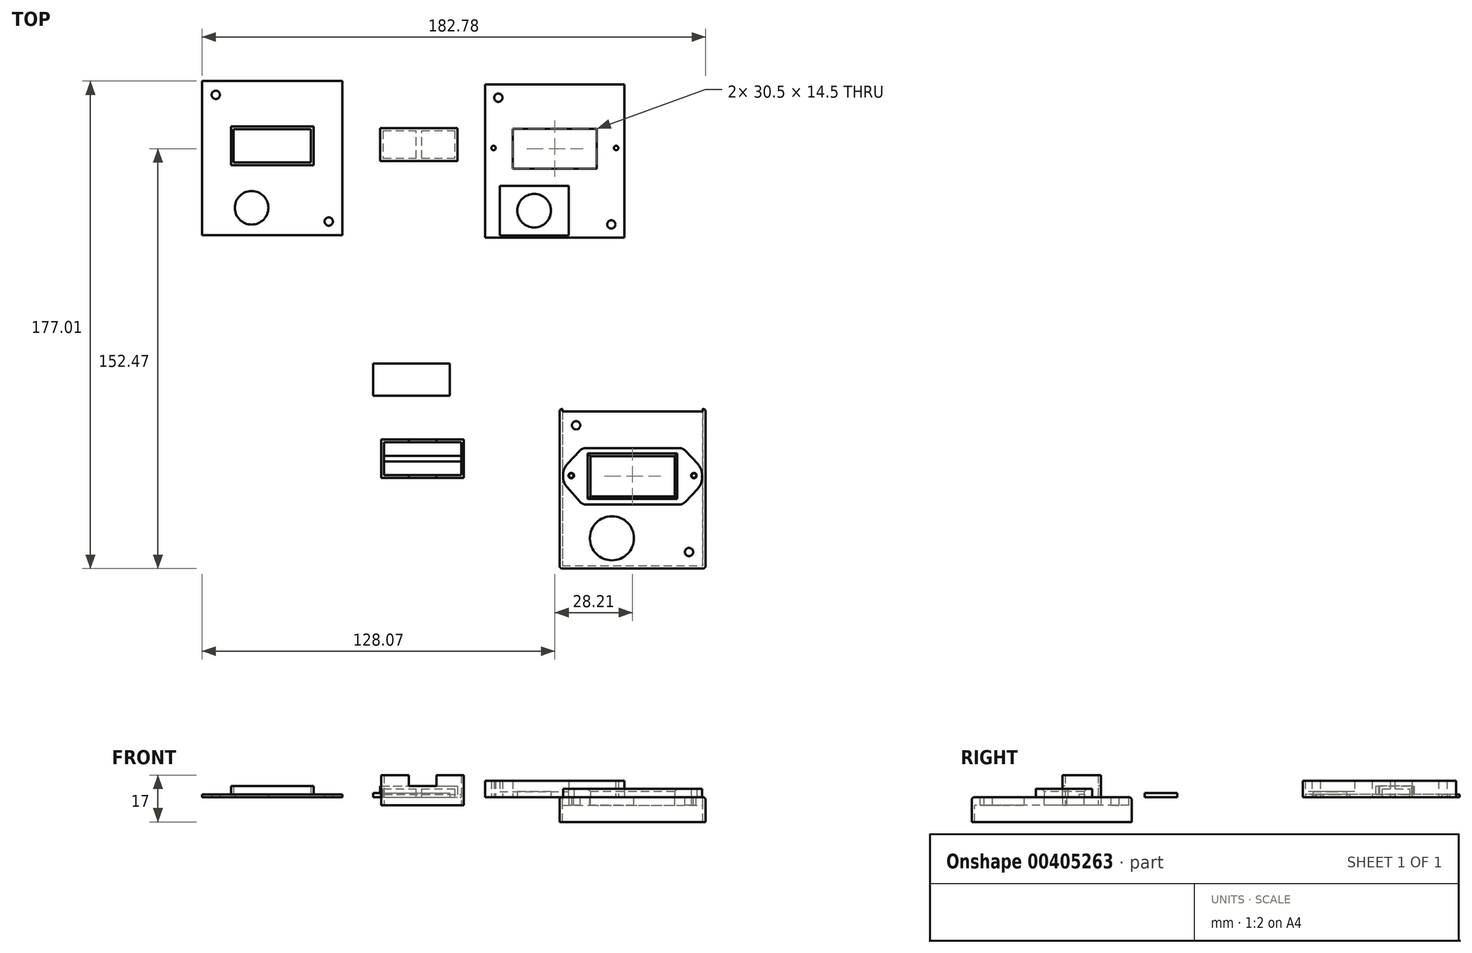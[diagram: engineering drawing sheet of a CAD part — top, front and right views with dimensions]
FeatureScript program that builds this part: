
annotation { "Feature Type Name" : "Feature", "Feature Type Description" : "" }
export const myFeature = defineFeature(function(context is Context, id is Id, definition is map)
    precondition{}
    {
        {
            var Q0;
            Q0=qCreatedBy(makeId("Top.planeOp"),FACE);
            var sketch = newSketch(context, id + "F0", { "sketchPlane" : qUnion([Q0])});
            skLineSegment(sketch, "E0.bottom", {"start": v(25.5, 28) * mm, "end": v(-25.5, 28) * mm});
            skLineSegment(sketch, "E0.top", {"start": v(25.5, -28) * mm, "end": v(-25.5, -28) * mm});
            skLineSegment(sketch, "E0.left", {"start": v(25.5, 28) * mm, "end": v(25.5, -28) * mm});
            skLineSegment(sketch, "E0.right", {"start": v(-25.5, 28) * mm, "end": v(-25.5, -28) * mm});
            skCircle(sketch, "E1", {"center": v(-20.5, 23) * mm, "radius": 1.5 * mm});
            skCircle(sketch, "E2", {"center": v(20.5, -23) * mm, "radius": 1.5 * mm});
            skCircle(sketch, "E3", {"center": v(-7.5, -18) * mm, "radius": 6.1 * mm});
            skLineSegment(sketch, "E4.bottom", {"start": v(-15.25, 11.75) * mm, "end": v(15.25, 11.75) * mm});
            skLineSegment(sketch, "E4.top", {"start": v(-15.25, -2.75) * mm, "end": v(15.25, -2.75) * mm});
            skLineSegment(sketch, "E4.left", {"start": v(-15.25, 11.75) * mm, "end": v(-15.25, -2.75) * mm});
            skLineSegment(sketch, "E4.right", {"start": v(15.25, 11.75) * mm, "end": v(15.25, -2.75) * mm});
            skPoint(sketch, "E5.middle", {"position": v(-103.8, -4.8) * mm});
            skLineSegment(sketch, "E6.bottom", {"start": v(-116.57, 11.54) * mm, "end": v(-88.57, 11.54) * mm});
            skLineSegment(sketch, "E6.top", {"start": v(-116.57, -0.46) * mm, "end": v(-88.57, -0.46) * mm});
            skLineSegment(sketch, "E6.left", {"start": v(-116.57, 11.54) * mm, "end": v(-116.57, -0.46) * mm});
            skLineSegment(sketch, "E6.right", {"start": v(-88.57, 11.54) * mm, "end": v(-88.57, -0.46) * mm});
            skLineSegment(sketch, "E7.bottom", {"start": v(-112.82, 11.54) * mm, "end": v(-110.32, 11.54) * mm});
            skLineSegment(sketch, "E7.top", {"start": v(-112.82, -0.46) * mm, "end": v(-110.32, -0.46) * mm});
            skLineSegment(sketch, "E7.left", {"start": v(-112.82, 11.54) * mm, "end": v(-112.82, -0.46) * mm});
            skLineSegment(sketch, "E7.right", {"start": v(-110.32, 11.54) * mm, "end": v(-110.32, -0.46) * mm});
            skLineSegment(sketch, "E8.bottom", {"start": v(-94.82, 11.54) * mm, "end": v(-92.32, 11.54) * mm});
            skLineSegment(sketch, "E8.top", {"start": v(-94.82, -0.46) * mm, "end": v(-92.32, -0.46) * mm});
            skLineSegment(sketch, "E8.left", {"start": v(-94.82, 11.54) * mm, "end": v(-94.82, -0.46) * mm});
            skLineSegment(sketch, "E8.right", {"start": v(-92.32, 11.54) * mm, "end": v(-92.32, -0.46) * mm});
            skLineSegment(sketch, "E9.bottom", {"start": v(-114.57, 8.54) * mm, "end": v(-108.57, 8.54) * mm, "construction": true});
            skLineSegment(sketch, "E9.top", {"start": v(-114.57, 2.54) * mm, "end": v(-108.57, 2.54) * mm, "construction": true});
            skLineSegment(sketch, "E9.left", {"start": v(-114.57, 8.54) * mm, "end": v(-114.57, 2.54) * mm, "construction": true});
            skLineSegment(sketch, "E9.right", {"start": v(-108.57, 8.54) * mm, "end": v(-108.57, 2.54) * mm, "construction": true});
            skLineSegment(sketch, "E10.bottom", {"start": v(-96.57, 8.54) * mm, "end": v(-90.57, 8.54) * mm, "construction": true});
            skLineSegment(sketch, "E10.top", {"start": v(-96.57, 2.54) * mm, "end": v(-90.57, 2.54) * mm, "construction": true});
            skLineSegment(sketch, "E10.left", {"start": v(-96.57, 8.54) * mm, "end": v(-96.57, 2.54) * mm, "construction": true});
            skLineSegment(sketch, "E10.right", {"start": v(-90.57, 8.54) * mm, "end": v(-90.57, 2.54) * mm, "construction": true});
            skLineSegment(sketch, "E11.bottom", {"start": v(-2.5, 11.75) * mm, "end": v(2.5, 11.75) * mm});
            skLineSegment(sketch, "E11.top", {"start": v(-2.5, -2.75) * mm, "end": v(2.5, -2.75) * mm});
            skLineSegment(sketch, "E11.left", {"start": v(-2.5, 11.75) * mm, "end": v(-2.5, -2.75) * mm});
            skLineSegment(sketch, "E11.right", {"start": v(2.5, 11.75) * mm, "end": v(2.5, -2.75) * mm});
            skLineSegment(sketch, "E12.bottom", {"start": v(-6.25, 10.5) * mm, "end": v(5.75, 10.5) * mm, "construction": true});
            skLineSegment(sketch, "E12.top", {"start": v(-6.25, -1.5) * mm, "end": v(5.75, -1.5) * mm, "construction": true});
            skLineSegment(sketch, "E12.left", {"start": v(-6.25, 10.5) * mm, "end": v(-6.25, -1.5) * mm, "construction": true});
            skLineSegment(sketch, "E12.right", {"start": v(5.75, 10.5) * mm, "end": v(5.75, -1.5) * mm, "construction": true});
            skLineSegment(sketch, "E13.bottom", {"start": v(-128.07, 29.04) * mm, "end": v(-77.07, 29.04) * mm});
            skLineSegment(sketch, "E13.top", {"start": v(-128.07, -26.96) * mm, "end": v(-77.07, -26.96) * mm});
            skLineSegment(sketch, "E13.left", {"start": v(-128.07, 29.04) * mm, "end": v(-128.07, -26.96) * mm});
            skLineSegment(sketch, "E13.right", {"start": v(-77.07, 29.04) * mm, "end": v(-77.07, -26.96) * mm});
            skCircle(sketch, "E14", {"center": v(-123.07, 24.04) * mm, "radius": 1.5 * mm});
            skCircle(sketch, "E15", {"center": v(-82.07, -21.96) * mm, "radius": 1.5 * mm});
            skLineSegment(sketch, "E16.bottom", {"start": v(-14, 10.5) * mm, "end": v(14, 10.5) * mm, "construction": true});
            skLineSegment(sketch, "E16.top", {"start": v(-14, -1.5) * mm, "end": v(14, -1.5) * mm, "construction": true});
            skLineSegment(sketch, "E16.left", {"start": v(-14, 10.5) * mm, "end": v(-14, -1.5) * mm, "construction": true});
            skLineSegment(sketch, "E16.right", {"start": v(14, 10.5) * mm, "end": v(14, -1.5) * mm, "construction": true});
            skCircle(sketch, "E17", {"center": v(-110.07, -16.96) * mm, "radius": 6.1 * mm});
            skSolve(sketch);
        }
        {
            var Q0;
            Q0=makeQuery(id+"F0.imprint","IMPRINT",FACE,{"disambiguationData":[TD([[makeQuery(id+"F0.imprint","IMPRINT",EDGE,{"derivedFrom":sQuery(id+"F0.wireOp",EDGE,"E0.bottom")}),1.0]])]});
            var Q1;
            Q1=makeQuery(id+"F0.imprint","IMPRINT",FACE,{"disambiguationData":[TD([[makeQuery(id+"F0.imprint","IMPRINT",EDGE,{"derivedFrom":sQuery(id+"F0.wireOp",EDGE,"LN2d2Qam-zQ4N-hJWI-jsZm-hQ2YjQqxJFMe.bottom")}),-1.0]])]});
            var Q2;
            Q2=makeQuery(id+"F0.imprint","IMPRINT",FACE,{"disambiguationData":[TD([[makeQuery(id+"F0.imprint","IMPRINT",EDGE,{"derivedFrom":sQuery(id+"F0.wireOp",EDGE,"Tyq8l7xN-NJ6r-rAiC-5Q4v-MCzvgNdMf9WX.bottom")}),-1.0]])]});
            var Q3;
            Q3=makeQuery(id+"F0.imprint","IMPRINT",FACE,{"disambiguationData":[TD([[makeQuery(id+"F0.imprint","IMPRINT",EDGE,{"derivedFrom":sQuery(id+"F0.wireOp",EDGE,"E11.bottom")}),-1.0]])]});
            var Q4;
            {var subQ12=sQuery(id+"F0.wireOp",EDGE,"E6.left");Q4=makeQuery(id+"F0.imprint","IMPRINT",FACE,{"disambiguationData":[TD([[makeQuery(id+"F0.imprint","IMPRINT",EDGE,{"derivedFrom":subQ12}),-1.0]])]});}
            var Q5;
            Q5=makeQuery(id+"F0.imprint","IMPRINT",FACE,{"disambiguationData":[TD([[makeQuery(id+"F0.imprint","IMPRINT",EDGE,{"derivedFrom":sQuery(id+"F0.wireOp",EDGE,"E7.bottom")}),-1.0]])]});
            var Q6;
            Q6=makeQuery(id+"F0.imprint","IMPRINT",FACE,{"disambiguationData":[TD([[makeQuery(id+"F0.imprint","IMPRINT",EDGE,{"derivedFrom":sQuery(id+"F0.wireOp",EDGE,"E8.bottom")}),-1.0]])]});
            var Q7;
            Q7=makeQuery(id+"F0.imprint","IMPRINT",FACE,{"disambiguationData":[TD([[makeQuery(id+"F0.imprint","IMPRINT",EDGE,{"derivedFrom":sQuery(id+"F0.wireOp",EDGE,"V3zyF6Pa-9TGi-MSfi-dUwD-Oto6uP0OLka4.bottom")}),-1.0]])]});
            extrude(context, id + "F1", {"entities" : qUnion([Q0, Q1, Q2, Q3, Q4, Q5, Q6, Q7]), "depth" : 1 * mm});
        }
        {
            var Q0;
            Q0=qCreatedBy(makeId("Top.planeOp"),FACE);
            var sketch = newSketch(context, id + "F2", { "sketchPlane" : qUnion([Q0])});
            skPoint(sketch, "E18.middle", {"position": v(28.78, -122.02) * mm});
            skLineSegment(sketch, "E19.bottom", {"start": v(14.21, -108.47) * mm, "end": v(42.21, -108.47) * mm, "construction": true});
            skLineSegment(sketch, "E19.top", {"start": v(14.21, -120.47) * mm, "end": v(42.21, -120.47) * mm, "construction": true});
            skLineSegment(sketch, "E19.left", {"start": v(14.21, -108.47) * mm, "end": v(14.21, -120.47) * mm, "construction": true});
            skLineSegment(sketch, "E19.right", {"start": v(42.21, -108.47) * mm, "end": v(42.21, -120.47) * mm, "construction": true});
            skLineSegment(sketch, "E20.bottom", {"start": v(20.96, -108.47) * mm, "end": v(23.46, -108.47) * mm, "construction": true});
            skLineSegment(sketch, "E20.top", {"start": v(20.96, -120.47) * mm, "end": v(23.46, -120.47) * mm, "construction": true});
            skLineSegment(sketch, "E20.left", {"start": v(20.96, -108.47) * mm, "end": v(20.96, -120.47) * mm, "construction": true});
            skLineSegment(sketch, "E20.right", {"start": v(23.46, -108.47) * mm, "end": v(23.46, -120.47) * mm, "construction": true});
            skLineSegment(sketch, "E21.bottom", {"start": v(32.96, -108.47) * mm, "end": v(35.46, -108.47) * mm, "construction": true});
            skLineSegment(sketch, "E21.top", {"start": v(32.96, -120.47) * mm, "end": v(35.46, -120.47) * mm, "construction": true});
            skLineSegment(sketch, "E21.left", {"start": v(32.96, -108.47) * mm, "end": v(32.96, -120.47) * mm, "construction": true});
            skLineSegment(sketch, "E21.right", {"start": v(35.46, -108.47) * mm, "end": v(35.46, -120.47) * mm, "construction": true});
            skLineSegment(sketch, "E22.bottom", {"start": v(19.21, -111.47) * mm, "end": v(25.21, -111.47) * mm, "construction": true});
            skLineSegment(sketch, "E22.top", {"start": v(19.21, -117.47) * mm, "end": v(25.21, -117.47) * mm, "construction": true});
            skLineSegment(sketch, "E22.left", {"start": v(19.21, -111.47) * mm, "end": v(19.21, -117.47) * mm, "construction": true});
            skLineSegment(sketch, "E22.right", {"start": v(25.21, -111.47) * mm, "end": v(25.21, -117.47) * mm, "construction": true});
            skLineSegment(sketch, "E23.bottom", {"start": v(31.21, -111.47) * mm, "end": v(37.21, -111.47) * mm, "construction": true});
            skLineSegment(sketch, "E23.top", {"start": v(31.21, -117.47) * mm, "end": v(37.21, -117.47) * mm, "construction": true});
            skLineSegment(sketch, "E23.left", {"start": v(31.21, -111.47) * mm, "end": v(31.21, -117.47) * mm, "construction": true});
            skLineSegment(sketch, "E23.right", {"start": v(37.21, -111.47) * mm, "end": v(37.21, -117.47) * mm, "construction": true});
            skLineSegment(sketch, "E24.bottom", {"start": v(2.71, -90.97) * mm, "end": v(53.71, -90.97) * mm});
            skLineSegment(sketch, "E24.top", {"start": v(2.71, -146.97) * mm, "end": v(53.71, -146.97) * mm});
            skLineSegment(sketch, "E24.left", {"start": v(2.71, -90.97) * mm, "end": v(2.71, -146.97) * mm});
            skLineSegment(sketch, "E24.right", {"start": v(53.71, -90.97) * mm, "end": v(53.71, -146.97) * mm});
            skCircle(sketch, "E25", {"center": v(7.71, -95.97) * mm, "radius": 1.5 * mm});
            skCircle(sketch, "E26", {"center": v(48.71, -141.97) * mm, "radius": 1.5 * mm});
            skCircle(sketch, "E27", {"center": v(20.71, -136.97) * mm, "radius": 8 * mm});
            skLineSegment(sketch, "E28.bottom", {"start": v(12.96, -107.22) * mm, "end": v(43.46, -107.22) * mm});
            skLineSegment(sketch, "E28.top", {"start": v(12.96, -121.72) * mm, "end": v(43.46, -121.72) * mm});
            skLineSegment(sketch, "E28.left", {"start": v(12.96, -107.22) * mm, "end": v(12.96, -121.72) * mm});
            skLineSegment(sketch, "E28.right", {"start": v(43.46, -107.22) * mm, "end": v(43.46, -121.72) * mm});
            skPoint(sketch, "E29.middle", {"position": v(-49.22, -118.43) * mm});
            skLineSegment(sketch, "E30.bottom", {"start": v(-62, -102.08) * mm, "end": v(-34, -102.08) * mm});
            skLineSegment(sketch, "E30.top", {"start": v(-62, -114.08) * mm, "end": v(-34, -114.08) * mm});
            skLineSegment(sketch, "E30.left", {"start": v(-62, -102.08) * mm, "end": v(-62, -114.08) * mm});
            skLineSegment(sketch, "E30.right", {"start": v(-34, -102.08) * mm, "end": v(-34, -114.08) * mm});
            skLineSegment(sketch, "E31.bottom", {"start": v(-57.25, -102.08) * mm, "end": v(-54.75, -102.08) * mm, "construction": true});
            skLineSegment(sketch, "E31.top", {"start": v(-57.25, -114.08) * mm, "end": v(-54.75, -114.08) * mm, "construction": true});
            skLineSegment(sketch, "E31.left", {"start": v(-57.25, -102.08) * mm, "end": v(-57.25, -114.08) * mm, "construction": true});
            skLineSegment(sketch, "E31.right", {"start": v(-54.75, -102.08) * mm, "end": v(-54.75, -114.08) * mm, "construction": true});
            skLineSegment(sketch, "E32.bottom", {"start": v(-41.25, -102.08) * mm, "end": v(-38.75, -102.08) * mm, "construction": true});
            skLineSegment(sketch, "E32.top", {"start": v(-41.25, -114.08) * mm, "end": v(-38.75, -114.08) * mm, "construction": true});
            skLineSegment(sketch, "E32.left", {"start": v(-41.25, -102.08) * mm, "end": v(-41.25, -114.08) * mm, "construction": true});
            skLineSegment(sketch, "E32.right", {"start": v(-38.75, -102.08) * mm, "end": v(-38.75, -114.08) * mm, "construction": true});
            skLineSegment(sketch, "E33.bottom", {"start": v(-59, -105.08) * mm, "end": v(-53, -105.08) * mm, "construction": true});
            skLineSegment(sketch, "E33.top", {"start": v(-59, -111.08) * mm, "end": v(-53, -111.08) * mm, "construction": true});
            skLineSegment(sketch, "E33.left", {"start": v(-59, -105.08) * mm, "end": v(-59, -111.08) * mm, "construction": true});
            skLineSegment(sketch, "E33.right", {"start": v(-53, -105.08) * mm, "end": v(-53, -111.08) * mm, "construction": true});
            skLineSegment(sketch, "E34.bottom", {"start": v(-43, -105.08) * mm, "end": v(-37, -105.08) * mm, "construction": true});
            skLineSegment(sketch, "E34.top", {"start": v(-43, -111.08) * mm, "end": v(-37, -111.08) * mm, "construction": true});
            skLineSegment(sketch, "E34.left", {"start": v(-43, -105.08) * mm, "end": v(-43, -111.08) * mm, "construction": true});
            skLineSegment(sketch, "E34.right", {"start": v(-37, -105.08) * mm, "end": v(-37, -111.08) * mm, "construction": true});
            skLineSegment(sketch, "E35.bottom", {"start": v(-63, -101.08) * mm, "end": v(-33, -101.08) * mm});
            skLineSegment(sketch, "E35.top", {"start": v(-63, -115.08) * mm, "end": v(-33, -115.08) * mm});
            skLineSegment(sketch, "E35.left", {"start": v(-63, -101.08) * mm, "end": v(-63, -115.08) * mm});
            skLineSegment(sketch, "E35.right", {"start": v(-33, -101.08) * mm, "end": v(-33, -115.08) * mm});
            skLineSegment(sketch, "E36.bottom", {"start": v(-62, -107.08) * mm, "end": v(-34, -107.08) * mm});
            skLineSegment(sketch, "E36.top", {"start": v(-62, -109.08) * mm, "end": v(-34, -109.08) * mm});
            skLineSegment(sketch, "E36.left", {"start": v(-62, -107.08) * mm, "end": v(-62, -109.08) * mm});
            skLineSegment(sketch, "E36.right", {"start": v(-34, -107.08) * mm, "end": v(-34, -109.08) * mm});
            skLineSegment(sketch, "E37.bottom", {"start": v(-53, -102.08) * mm, "end": v(-43, -102.08) * mm});
            skLineSegment(sketch, "E37.top", {"start": v(-53, -114.08) * mm, "end": v(-43, -114.08) * mm});
            skLineSegment(sketch, "E37.left", {"start": v(-53, -102.08) * mm, "end": v(-53, -114.08) * mm});
            skLineSegment(sketch, "E37.right", {"start": v(-43, -102.08) * mm, "end": v(-43, -114.08) * mm});
            skLineSegment(sketch, "E38.top", {"start": v(2.71, -89.97) * mm, "end": v(53.71, -89.97) * mm});
            skLineSegment(sketch, "E38.left", {"start": v(2.71, -90.97) * mm, "end": v(2.71, -89.97) * mm});
            skLineSegment(sketch, "E38.right", {"start": v(53.71, -90.97) * mm, "end": v(53.71, -89.97) * mm});
            skLineSegment(sketch, "E39.top", {"start": v(2.71, -147.97) * mm, "end": v(53.71, -147.97) * mm});
            skLineSegment(sketch, "E39.left", {"start": v(2.71, -146.97) * mm, "end": v(2.71, -147.97) * mm});
            skLineSegment(sketch, "E39.right", {"start": v(53.71, -146.97) * mm, "end": v(53.71, -147.97) * mm});
            skLineSegment(sketch, "E40.bottom", {"start": v(53.71, -89.97) * mm, "end": v(54.71, -89.97) * mm});
            skLineSegment(sketch, "E40.top", {"start": v(53.71, -147.97) * mm, "end": v(54.71, -147.97) * mm});
            skLineSegment(sketch, "E40.left", {"start": v(53.71, -89.97) * mm, "end": v(53.71, -147.97) * mm});
            skLineSegment(sketch, "E40.right", {"start": v(54.71, -89.97) * mm, "end": v(54.71, -147.97) * mm});
            skLineSegment(sketch, "E41.bottom", {"start": v(2.71, -89.97) * mm, "end": v(1.71, -89.97) * mm});
            skLineSegment(sketch, "E41.top", {"start": v(2.71, -147.97) * mm, "end": v(1.71, -147.97) * mm});
            skLineSegment(sketch, "E41.left", {"start": v(2.71, -89.97) * mm, "end": v(2.71, -147.97) * mm});
            skLineSegment(sketch, "E41.right", {"start": v(1.71, -89.97) * mm, "end": v(1.71, -147.97) * mm});
            skCircle(sketch, "E42", {"center": v(5.96, -114.22) * mm, "radius": 0.8 * mm});
            skCircle(sketch, "E43", {"center": v(50.46, -114.22) * mm, "radius": 0.8 * mm});
            skSolve(sketch);
        }
        {
            var Q0;
            Q0=makeQuery(id+"F1.opExtrude","CAP_FACE",FACE,{"disambiguationData":[OSD([sQuery(id+"F0.wireOp",EDGE,"E6.bottom"),sQuery(id+"F0.wireOp",EDGE,"E6.top"),sQuery(id+"F0.wireOp",EDGE,"E6.left"),sQuery(id+"F0.wireOp",EDGE,"E6.right"),sQuery(id+"F0.wireOp",EDGE,"E7.left"),sQuery(id+"F0.wireOp",EDGE,"E7.right"),sQuery(id+"F0.wireOp",EDGE,"E8.left"),sQuery(id+"F0.wireOp",EDGE,"E8.right"),sQuery(id+"F0.wireOp",EDGE,"E13.bottom"),sQuery(id+"F0.wireOp",EDGE,"E13.top"),sQuery(id+"F0.wireOp",EDGE,"E13.left"),sQuery(id+"F0.wireOp",EDGE,"E13.right"),sQuery(id+"F0.wireOp",EDGE,"E14"),sQuery(id+"F0.wireOp",EDGE,"E15"),sQuery(id+"F0.wireOp",EDGE,"E17"),sQuery(id+"F0.wireOp",EDGE,"V3zyF6Pa-9TGi-MSfi-dUwD-Oto6uP0OLka4.left"),sQuery(id+"F0.wireOp",EDGE,"V3zyF6Pa-9TGi-MSfi-dUwD-Oto6uP0OLka4.right")])],"isStart":false});
            var sketch = newSketch(context, id + "F3", { "sketchPlane" : qUnion([Q0])});
            skLineSegment(sketch, "E44.bottom", {"start": v(-116.57, 11.54) * mm, "end": v(-88.57, 11.54) * mm});
            skLineSegment(sketch, "E44.top", {"start": v(-116.57, 12.54) * mm, "end": v(-88.57, 12.54) * mm});
            skLineSegment(sketch, "E44.left", {"start": v(-116.57, 11.54) * mm, "end": v(-116.57, 12.54) * mm});
            skLineSegment(sketch, "E44.right", {"start": v(-88.57, 11.54) * mm, "end": v(-88.57, 12.54) * mm});
            skLineSegment(sketch, "E45.bottom", {"start": v(-116.57, -0.46) * mm, "end": v(-88.57, -0.46) * mm});
            skLineSegment(sketch, "E45.top", {"start": v(-116.57, -1.46) * mm, "end": v(-88.57, -1.46) * mm});
            skLineSegment(sketch, "E45.left", {"start": v(-116.57, -0.46) * mm, "end": v(-116.57, -1.46) * mm});
            skLineSegment(sketch, "E45.right", {"start": v(-88.57, -0.46) * mm, "end": v(-88.57, -1.46) * mm});
            skLineSegment(sketch, "E46.bottom", {"start": v(-116.57, -1.46) * mm, "end": v(-117.57, -1.46) * mm});
            skLineSegment(sketch, "E46.top", {"start": v(-116.57, 12.54) * mm, "end": v(-117.57, 12.54) * mm});
            skLineSegment(sketch, "E46.left", {"start": v(-116.57, -1.46) * mm, "end": v(-116.57, 12.54) * mm});
            skLineSegment(sketch, "E46.right", {"start": v(-117.57, -1.46) * mm, "end": v(-117.57, 12.54) * mm});
            skLineSegment(sketch, "E47.bottom", {"start": v(-88.57, 12.54) * mm, "end": v(-87.57, 12.54) * mm});
            skLineSegment(sketch, "E47.top", {"start": v(-88.57, -1.46) * mm, "end": v(-87.57, -1.46) * mm});
            skLineSegment(sketch, "E47.left", {"start": v(-88.57, 12.54) * mm, "end": v(-88.57, -1.46) * mm});
            skLineSegment(sketch, "E47.right", {"start": v(-87.57, 12.54) * mm, "end": v(-87.57, -1.46) * mm});
            skSolve(sketch);
        }
        {
            var Q0;
            Q0=qSketchRegion(id+"F3",true);
            extrude(context, id + "F4", {"entities" : qUnion([Q0]), "operationType" : NewBodyOperationType.ADD, "depth" : 3 * mm});
        }
        {
            var Q0;
            Q0=qCreatedBy(makeId("Top.planeOp"),FACE);
            var sketch = newSketch(context, id + "F5", { "sketchPlane" : qUnion([Q0])});
            skLineSegment(sketch, "E48.bottom", {"start": v(-63.36, 12) * mm, "end": v(-35.36, 12) * mm});
            skLineSegment(sketch, "E48.top", {"start": v(-63.36, 0) * mm, "end": v(-35.36, 0) * mm});
            skLineSegment(sketch, "E48.left", {"start": v(-63.36, 12) * mm, "end": v(-63.36, 0) * mm});
            skLineSegment(sketch, "E48.right", {"start": v(-35.36, 12) * mm, "end": v(-35.36, 0) * mm});
            skLineSegment(sketch, "E49.bottom", {"start": v(-65.94, -73.47) * mm, "end": v(-38.14, -73.47) * mm});
            skLineSegment(sketch, "E49.top", {"start": v(-65.94, -85.27) * mm, "end": v(-38.14, -85.27) * mm});
            skLineSegment(sketch, "E49.left", {"start": v(-65.94, -73.47) * mm, "end": v(-65.94, -85.27) * mm});
            skLineSegment(sketch, "E49.right", {"start": v(-38.14, -73.47) * mm, "end": v(-38.14, -85.27) * mm});
            skSolve(sketch);
        }
        {
            var Q0;
            Q0=makeQuery(id+"F5.imprint","IMPRINT",FACE,{"disambiguationData":[TD([[makeQuery(id+"F5.imprint","IMPRINT",EDGE,{"derivedFrom":sQuery(id+"F5.wireOp",EDGE,"E48.bottom")}),-1.0]])]});
            extrude(context, id + "F6", {"entities" : qUnion([Q0]), "depth" : 4 * mm});
        }
        {
            var Q0;
            Q0=makeQuery(id+"F6.opExtrude","CAP_FACE",FACE,{"disambiguationData":[OSD([sQuery(id+"F5.wireOp",EDGE,"E48.bottom"),sQuery(id+"F5.wireOp",EDGE,"E48.top"),sQuery(id+"F5.wireOp",EDGE,"E48.left"),sQuery(id+"F5.wireOp",EDGE,"E48.right")])],"isStart":true});
            shell(context, id + "F7", {"entities" : qUnion([Q0]), "thickness" : 1 * mm});
        }
        {
            var Q0;
            Q0=makeQuery(id+"F7.opShell","OFFSET_FACE",FACE,{"disambiguationData":[OSD([sQuery(id+"F5.wireOp",EDGE,"E48.bottom"),sQuery(id+"F5.wireOp",EDGE,"E48.top"),sQuery(id+"F5.wireOp",EDGE,"E48.left"),sQuery(id+"F5.wireOp",EDGE,"E48.right")])]});
            var sketch = newSketch(context, id + "F8", { "sketchPlane" : qUnion([Q0])});
            skLineSegment(sketch, "E50.bottom", {"start": v(-50.36, -1) * mm, "end": v(-48.36, -1) * mm});
            skLineSegment(sketch, "E50.top", {"start": v(-50.36, -11) * mm, "end": v(-48.36, -11) * mm});
            skLineSegment(sketch, "E50.left", {"start": v(-50.36, -1) * mm, "end": v(-50.36, -11) * mm});
            skLineSegment(sketch, "E50.right", {"start": v(-48.36, -1) * mm, "end": v(-48.36, -11) * mm});
            skSolve(sketch);
        }
        {
            var Q0;
            Q0=makeQuery(id+"F8.imprint","IMPRINT",FACE,{"disambiguationData":[TD([[makeQuery(id+"F8.imprint","IMPRINT",EDGE,{"derivedFrom":sQuery(id+"F8.wireOp",EDGE,"E50.bottom")}),-1.0]])]});
            extrude(context, id + "F9", {"entities" : qUnion([Q0]), "operationType" : NewBodyOperationType.ADD, "depth" : 3 * mm});
        }
        {
            var Q0;
            Q0=makeQuery(id+"F1.opExtrude","CAP_FACE",FACE,{"disambiguationData":[OSD([sQuery(id+"F0.wireOp",EDGE,"E0.bottom"),sQuery(id+"F0.wireOp",EDGE,"E0.top"),sQuery(id+"F0.wireOp",EDGE,"E0.left"),sQuery(id+"F0.wireOp",EDGE,"E0.right"),sQuery(id+"F0.wireOp",EDGE,"E1"),sQuery(id+"F0.wireOp",EDGE,"E2"),sQuery(id+"F0.wireOp",EDGE,"E3"),sQuery(id+"F0.wireOp",EDGE,"E4.bottom"),sQuery(id+"F0.wireOp",EDGE,"E4.top"),sQuery(id+"F0.wireOp",EDGE,"E4.left"),sQuery(id+"F0.wireOp",EDGE,"E4.right"),sQuery(id+"F0.wireOp",EDGE,"E11.left"),sQuery(id+"F0.wireOp",EDGE,"E11.right")])],"isStart":false});
            var sketch = newSketch(context, id + "F10", { "sketchPlane" : qUnion([Q0])});
            skLineSegment(sketch, "E51.bottom", {"start": v(-6.25, 10.25) * mm, "end": v(5.75, 10.25) * mm, "construction": true});
            skLineSegment(sketch, "E51.top", {"start": v(-6.25, -1.75) * mm, "end": v(5.75, -1.75) * mm, "construction": true});
            skLineSegment(sketch, "E51.left", {"start": v(-6.25, 10.25) * mm, "end": v(-6.25, -1.75) * mm, "construction": true});
            skLineSegment(sketch, "E51.right", {"start": v(5.75, 10.25) * mm, "end": v(5.75, -1.75) * mm, "construction": true});
            skSolve(sketch);
        }
        {
            var Q0;
            {var subQ3=sQuery(id+"F2.wireOp",EDGE,"E30.left");Q0=makeQuery(id+"F2.imprint","IMPRINT",FACE,{"disambiguationData":[TD([[makeQuery(id+"F2.imprint","IMPRINT",EDGE,{"derivedFrom":subQ3}),-1.0]])]});}
            extrude(context, id + "F11", {"entities" : qUnion([Q0]), "depth" : 4 * mm});
        }
        {
            var Q0;
            Q0=makeQuery(id+"F2.imprint","IMPRINT",FACE,{"disambiguationData":[TD([[makeQuery(id+"F2.imprint","IMPRINT",EDGE,{"derivedFrom":sQuery(id+"F2.wireOp",EDGE,"E25")}),-1.0]])]});
            extrude(context, id + "F12", {"entities" : qUnion([Q0]), "oppositeDirection" : true, "depth" : 3 * mm});
        }
        {
            var Q0;
            Q0=makeQuery(id+"F2.imprint","IMPRINT",FACE,{"disambiguationData":[TD([[makeQuery(id+"F2.imprint","IMPRINT",EDGE,{"derivedFrom":sQuery(id+"F2.wireOp",EDGE,"E36.bottom")}),-1.0]])]});
            var Q1;
            {var subQ5=sQuery(id+"F2.wireOp",EDGE,"E37.bottom");Q1=makeQuery(id+"F2.imprint","IMPRINT",FACE,{"disambiguationData":[TD([[makeQuery(id+"F2.imprint","IMPRINT",EDGE,{"derivedFrom":subQ5}),-1.0]])]});}
            var Q2;
            {var subQ5=sQuery(id+"F2.wireOp",EDGE,"E37.top");Q2=makeQuery(id+"F2.imprint","IMPRINT",FACE,{"disambiguationData":[TD([[makeQuery(id+"F2.imprint","IMPRINT",EDGE,{"derivedFrom":subQ5}),1.0]])]});}
            extrude(context, id + "F13", {"entities" : qUnion([Q0, Q1, Q2]), "operationType" : NewBodyOperationType.ADD, "depth" : 1 * mm});
        }
        {
            var Q0;
            Q0=makeQuery(id+"F5.imprint","IMPRINT",FACE,{"disambiguationData":[TD([[makeQuery(id+"F5.imprint","IMPRINT",EDGE,{"derivedFrom":sQuery(id+"F5.wireOp",EDGE,"E49.bottom")}),-1.0]])]});
            extrude(context, id + "F14", {"entities" : qUnion([Q0]), "depth" : 1.5 * mm});
        }
        {
            var Q0;
            {var subQ3=sQuery(id+"F2.wireOp",EDGE,"E41.bottom");Q0=makeQuery(id+"F2.imprint","IMPRINT",FACE,{"disambiguationData":[TD([[makeQuery(id+"F2.imprint","IMPRINT",EDGE,{"derivedFrom":subQ3}),1.0]])]});}
            var Q1;
            {var subQ0=sQuery(id+"F2.wireOp",EDGE,"E24.bottom");Q1=makeQuery(id+"F2.imprint","IMPRINT",FACE,{"disambiguationData":[TD([[makeQuery(id+"F2.imprint","IMPRINT",EDGE,{"derivedFrom":subQ0}),1.0]])]});}
            var Q2;
            {var subQ0=sQuery(id+"F2.wireOp",EDGE,"E24.top");Q2=makeQuery(id+"F2.imprint","IMPRINT",FACE,{"disambiguationData":[TD([[makeQuery(id+"F2.imprint","IMPRINT",EDGE,{"derivedFrom":subQ0}),-1.0]])]});}
            var Q3;
            {var subQ3=sQuery(id+"F2.wireOp",EDGE,"E40.bottom");Q3=makeQuery(id+"F2.imprint","IMPRINT",FACE,{"disambiguationData":[TD([[makeQuery(id+"F2.imprint","IMPRINT",EDGE,{"derivedFrom":subQ3}),-1.0]])]});}
            extrude(context, id + "F15", {"entities" : qUnion([Q0, Q1, Q2, Q3]), "operationType" : NewBodyOperationType.ADD, "oppositeDirection" : true, "depth" : 9 * mm});
        }
        {
            var Q0;
            Q0=makeQuery(id+"F2.imprint","IMPRINT",FACE,{"disambiguationData":[TD([[makeQuery(id+"F2.imprint","IMPRINT",EDGE,{"derivedFrom":sQuery(id+"F2.wireOp",EDGE,"E25")}),-1.0]])]});
            var sketch = newSketch(context, id + "F16", { "sketchPlane" : qUnion([Q0])});
            skLineSegment(sketch, "E52.bottom", {"start": v(9.96, -104.22) * mm, "end": v(46.46, -104.22) * mm});
            skLineSegment(sketch, "E52.top", {"start": v(9.96, -124.72) * mm, "end": v(46.46, -124.72) * mm});
            skLineSegment(sketch, "E52.left", {"start": v(9.96, -104.22) * mm, "end": v(9.96, -124.72) * mm});
            skLineSegment(sketch, "E52.right", {"start": v(46.46, -104.22) * mm, "end": v(46.46, -124.72) * mm});
            skLineSegment(sketch, "E53", {"start": v(9.96, -124.72) * mm, "end": v(2.96, -116.72) * mm});
            skLineSegment(sketch, "E54", {"start": v(2.96, -116.72) * mm, "end": v(2.96, -111.72) * mm});
            skLineSegment(sketch, "E55", {"start": v(2.96, -111.72) * mm, "end": v(9.96, -104.22) * mm});
            skCircle(sketch, "E56", {"center": v(5.96, -114.22) * mm, "radius": 1 * mm});
            skLineSegment(sketch, "E57.bottom", {"start": v(12.96, -107.22) * mm, "end": v(43.46, -107.22) * mm});
            skLineSegment(sketch, "E57.top", {"start": v(12.96, -121.72) * mm, "end": v(43.46, -121.72) * mm});
            skLineSegment(sketch, "E57.left", {"start": v(12.96, -107.22) * mm, "end": v(12.96, -121.72) * mm});
            skLineSegment(sketch, "E57.right", {"start": v(43.46, -107.22) * mm, "end": v(43.46, -121.72) * mm});
            skLineSegment(sketch, "E58", {"start": v(46.46, -104.22) * mm, "end": v(53.46, -111.72) * mm});
            skLineSegment(sketch, "E59", {"start": v(53.46, -111.72) * mm, "end": v(53.46, -117.22) * mm});
            skLineSegment(sketch, "E60", {"start": v(53.46, -117.22) * mm, "end": v(46.46, -124.72) * mm});
            skCircle(sketch, "E61", {"center": v(50.46, -114.22) * mm, "radius": 1 * mm});
            skSolve(sketch);
        }
        {
            var Q0;
            Q0=qSketchRegion(id+"F16",true);
            extrude(context, id + "F17", {"entities" : qUnion([Q0]), "depth" : 3 * mm});
        }
        {
            var Q0;
            Q0=makeQuery(id+"F17.opExtrude","SWEPT_EDGE",EDGE,{"disambiguationData":[OSD([sQuery(id+"F16.wireOp",EDGE,"E54"),sQuery(id+"F16.wireOp",EDGE,"E55")])]});
            var Q1;
            Q1=makeQuery(id+"F17.opExtrude","SWEPT_EDGE",EDGE,{"disambiguationData":[OSD([sQuery(id+"F16.wireOp",EDGE,"E53"),sQuery(id+"F16.wireOp",EDGE,"E54")])]});
            var Q2;
            Q2=makeQuery(id+"F17.opExtrude","SWEPT_EDGE",EDGE,{"disambiguationData":[OSD([sQuery(id+"F16.wireOp",EDGE,"E59"),sQuery(id+"F16.wireOp",EDGE,"E60")])]});
            var Q3;
            Q3=makeQuery(id+"F17.opExtrude","SWEPT_EDGE",EDGE,{"disambiguationData":[OSD([sQuery(id+"F16.wireOp",EDGE,"E58"),sQuery(id+"F16.wireOp",EDGE,"E59")])]});
            fillet(context, id + "F18", {"entities" : qUnion([Q0, Q1, Q2, Q3]), "radius" : 6 * mm, "tangentPropagation" : true, "allowEdgeOverflow" : false});
        }
        {
            var Q0;
            Q0=makeQuery(id+"F17.opExtrude","SWEPT_EDGE",EDGE,{"disambiguationData":[OSD([sQuery(id+"F16.wireOp",EDGE,"E52.bottom"),sQuery(id+"F16.wireOp",EDGE,"E52.left"),sQuery(id+"F16.wireOp",EDGE,"E55")])]});
            var Q1;
            Q1=makeQuery(id+"F17.opExtrude","SWEPT_EDGE",EDGE,{"disambiguationData":[OSD([sQuery(id+"F16.wireOp",EDGE,"E52.top"),sQuery(id+"F16.wireOp",EDGE,"E52.left"),sQuery(id+"F16.wireOp",EDGE,"E53")])]});
            var Q2;
            Q2=makeQuery(id+"F17.opExtrude","SWEPT_EDGE",EDGE,{"disambiguationData":[OSD([sQuery(id+"F16.wireOp",EDGE,"E52.top"),sQuery(id+"F16.wireOp",EDGE,"E52.right"),sQuery(id+"F16.wireOp",EDGE,"E60")])]});
            var Q3;
            Q3=makeQuery(id+"F17.opExtrude","SWEPT_EDGE",EDGE,{"disambiguationData":[OSD([sQuery(id+"F16.wireOp",EDGE,"E52.bottom"),sQuery(id+"F16.wireOp",EDGE,"E52.right"),sQuery(id+"F16.wireOp",EDGE,"E58")])]});
            fillet(context, id + "F19", {"entities" : qUnion([Q0, Q1, Q2, Q3]), "radius" : 3 * mm, "tangentPropagation" : true, "allowEdgeOverflow" : false});
        }
        {
            var Q0;
            Q0=makeQuery(id+"F15.opExtrude","CAP_EDGE",EDGE,{"disambiguationData":[OSD([sQuery(id+"F2.wireOp",EDGE,"E41.right")])],"isStart":true});
            var Q1;
            Q1=makeQuery(id+"F15.opExtrude","CAP_EDGE",EDGE,{"disambiguationData":[OSD([sQuery(id+"F2.wireOp",EDGE,"E38.top"),sQuery(id+"F2.wireOp",EDGE,"E40.bottom"),sQuery(id+"F2.wireOp",EDGE,"E41.bottom")])],"isStart":true});
            var Q2;
            Q2=makeQuery(id+"F15.opExtrude","CAP_EDGE",EDGE,{"disambiguationData":[OSD([sQuery(id+"F2.wireOp",EDGE,"E39.top"),sQuery(id+"F2.wireOp",EDGE,"E40.top"),sQuery(id+"F2.wireOp",EDGE,"E41.top")])],"isStart":true});
            var Q3;
            Q3=makeQuery(id+"F15.opExtrude","CAP_EDGE",EDGE,{"disambiguationData":[OSD([sQuery(id+"F2.wireOp",EDGE,"E40.right")])],"isStart":true});
            var Q4;
            Q4=makeQuery(id+"F15.opExtrude","SWEPT_EDGE",EDGE,{"disambiguationData":[OSD([sQuery(id+"F2.wireOp",EDGE,"E40.top"),sQuery(id+"F2.wireOp",EDGE,"E40.right")])]});
            var Q5;
            Q5=makeQuery(id+"F15.opExtrude","SWEPT_EDGE",EDGE,{"disambiguationData":[OSD([sQuery(id+"F2.wireOp",EDGE,"E41.top"),sQuery(id+"F2.wireOp",EDGE,"E41.right")])]});
            var Q6;
            Q6=makeQuery(id+"F15.opExtrude","SWEPT_EDGE",EDGE,{"disambiguationData":[OSD([sQuery(id+"F2.wireOp",EDGE,"E41.bottom"),sQuery(id+"F2.wireOp",EDGE,"E41.right")])]});
            var Q7;
            Q7=makeQuery(id+"F15.opExtrude","SWEPT_EDGE",EDGE,{"disambiguationData":[OSD([sQuery(id+"F2.wireOp",EDGE,"E40.bottom"),sQuery(id+"F2.wireOp",EDGE,"E40.right")])]});
            fillet(context, id + "F20", {"entities" : qUnion([Q0, Q1, Q2, Q3, Q4, Q5, Q6, Q7]), "radius" : 1 * mm, "tangentPropagation" : true, "allowEdgeOverflow" : false});
        }
        {
            var Q0;
            Q0=makeQuery(id+"F17.opExtrude","CAP_EDGE",EDGE,{"disambiguationData":[OSD([sQuery(id+"F16.wireOp",EDGE,"E57.left")])],"isStart":false});
            var Q1;
            Q1=makeQuery(id+"F17.opExtrude","CAP_EDGE",EDGE,{"disambiguationData":[OSD([sQuery(id+"F16.wireOp",EDGE,"E57.bottom")])],"isStart":false});
            var Q2;
            Q2=makeQuery(id+"F17.opExtrude","CAP_EDGE",EDGE,{"disambiguationData":[OSD([sQuery(id+"F16.wireOp",EDGE,"E57.right")])],"isStart":false});
            var Q3;
            Q3=makeQuery(id+"F17.opExtrude","CAP_EDGE",EDGE,{"disambiguationData":[OSD([sQuery(id+"F16.wireOp",EDGE,"E57.top")])],"isStart":false});
            chamfer(context, id + "F21", {"entities" : qUnion([Q0, Q1, Q2, Q3]), "width" : 1 * mm, "tangentPropagation" : true});
        }
        {
            var Q0;
            Q0=makeQuery(id+"F1.opExtrude","CAP_FACE",FACE,{"disambiguationData":[OSD([sQuery(id+"F0.wireOp",EDGE,"E0.bottom"),sQuery(id+"F0.wireOp",EDGE,"E0.top"),sQuery(id+"F0.wireOp",EDGE,"E0.left"),sQuery(id+"F0.wireOp",EDGE,"E0.right"),sQuery(id+"F0.wireOp",EDGE,"E1"),sQuery(id+"F0.wireOp",EDGE,"E2"),sQuery(id+"F0.wireOp",EDGE,"E3"),sQuery(id+"F0.wireOp",EDGE,"E4.bottom"),sQuery(id+"F0.wireOp",EDGE,"E4.top"),sQuery(id+"F0.wireOp",EDGE,"E4.left"),sQuery(id+"F0.wireOp",EDGE,"E4.right"),sQuery(id+"F0.wireOp",EDGE,"E11.left"),sQuery(id+"F0.wireOp",EDGE,"E11.right")])],"isStart":false});
            var sketch = newSketch(context, id + "F22", { "sketchPlane" : qUnion([Q0])});
            skCircle(sketch, "E62", {"center": v(-20.5, 23) * mm, "radius": 1.5 * mm});
            skCircle(sketch, "E63", {"center": v(20.5, -23) * mm, "radius": 1.5 * mm});
            skCircle(sketch, "E64", {"center": v(-7.5, -18) * mm, "radius": 8.5 * mm, "construction": true});
            skLineSegment(sketch, "E65.bottom", {"start": v(-25.5, 28) * mm, "end": v(25.5, 28) * mm});
            skLineSegment(sketch, "E65.top", {"start": v(-25.5, -28) * mm, "end": v(25.5, -28) * mm});
            skLineSegment(sketch, "E65.left", {"start": v(-25.5, 28) * mm, "end": v(-25.5, -28) * mm});
            skLineSegment(sketch, "E65.right", {"start": v(25.5, 28) * mm, "end": v(25.5, -28) * mm});
            skLineSegment(sketch, "E66.bottom", {"start": v(-15.25, 11.75) * mm, "end": v(15.25, 11.75) * mm});
            skLineSegment(sketch, "E66.top", {"start": v(-15.25, -2.75) * mm, "end": v(15.25, -2.75) * mm});
            skLineSegment(sketch, "E66.left", {"start": v(-15.25, 11.75) * mm, "end": v(-15.25, -2.75) * mm});
            skLineSegment(sketch, "E66.right", {"start": v(15.25, 11.75) * mm, "end": v(15.25, -2.75) * mm});
            skCircle(sketch, "E67", {"center": v(-22.25, 4.75) * mm, "radius": 2 * mm, "construction": true});
            skCircle(sketch, "E68", {"center": v(22.25, 4.75) * mm, "radius": 2 * mm, "construction": true});
            skLineSegment(sketch, "E69.bottom", {"start": v(5, -27) * mm, "end": v(-20, -27) * mm});
            skLineSegment(sketch, "E69.top", {"start": v(5, -9) * mm, "end": v(-20, -9) * mm});
            skLineSegment(sketch, "E69.left", {"start": v(5, -27) * mm, "end": v(5, -9) * mm});
            skLineSegment(sketch, "E69.right", {"start": v(-20, -27) * mm, "end": v(-20, -9) * mm});
            skSolve(sketch);
        }
        {
            var Q0;
            Q0=makeQuery(id+"F11.opExtrude","CAP_FACE",FACE,{"disambiguationData":[OSD([sQuery(id+"F2.wireOp",EDGE,"E30.bottom"),sQuery(id+"F2.wireOp",EDGE,"E30.top"),sQuery(id+"F2.wireOp",EDGE,"E30.left"),sQuery(id+"F2.wireOp",EDGE,"E30.right"),sQuery(id+"F2.wireOp",EDGE,"E35.bottom"),sQuery(id+"F2.wireOp",EDGE,"E35.top"),sQuery(id+"F2.wireOp",EDGE,"E35.left"),sQuery(id+"F2.wireOp",EDGE,"E35.right"),sQuery(id+"F2.wireOp",EDGE,"E36.left"),sQuery(id+"F2.wireOp",EDGE,"E36.right"),sQuery(id+"F2.wireOp",EDGE,"E37.bottom"),sQuery(id+"F2.wireOp",EDGE,"E37.top")])],"isStart":false});
            var sketch = newSketch(context, id + "F23", { "sketchPlane" : qUnion([Q0])});
            skLineSegment(sketch, "E70.bottom", {"start": v(-63, -101.08) * mm, "end": v(-53, -101.08) * mm});
            skLineSegment(sketch, "E70.top", {"start": v(-63, -102.08) * mm, "end": v(-53, -102.08) * mm});
            skLineSegment(sketch, "E70.left", {"start": v(-63, -101.08) * mm, "end": v(-63, -102.08) * mm});
            skLineSegment(sketch, "E70.right", {"start": v(-53, -101.08) * mm, "end": v(-53, -102.08) * mm});
            skLineSegment(sketch, "E71.bottom", {"start": v(-63, -102.08) * mm, "end": v(-62, -102.08) * mm});
            skLineSegment(sketch, "E71.top", {"start": v(-63, -115.08) * mm, "end": v(-62, -115.08) * mm});
            skLineSegment(sketch, "E71.left", {"start": v(-63, -102.08) * mm, "end": v(-63, -115.08) * mm});
            skLineSegment(sketch, "E71.right", {"start": v(-62, -102.08) * mm, "end": v(-62, -115.08) * mm});
            skLineSegment(sketch, "E72.bottom", {"start": v(-53, -114.08) * mm, "end": v(-62, -114.08) * mm});
            skLineSegment(sketch, "E72.top", {"start": v(-53, -115.08) * mm, "end": v(-62, -115.08) * mm});
            skLineSegment(sketch, "E72.left", {"start": v(-53, -114.08) * mm, "end": v(-53, -115.08) * mm});
            skLineSegment(sketch, "E72.right", {"start": v(-62, -114.08) * mm, "end": v(-62, -115.08) * mm});
            skLineSegment(sketch, "E73.bottom", {"start": v(-33, -101.08) * mm, "end": v(-43, -101.08) * mm});
            skLineSegment(sketch, "E73.top", {"start": v(-33, -102.08) * mm, "end": v(-43, -102.08) * mm});
            skLineSegment(sketch, "E73.left", {"start": v(-33, -101.08) * mm, "end": v(-33, -102.08) * mm});
            skLineSegment(sketch, "E73.right", {"start": v(-43, -101.08) * mm, "end": v(-43, -102.08) * mm});
            skLineSegment(sketch, "E74.bottom", {"start": v(-33, -102.08) * mm, "end": v(-34, -102.08) * mm});
            skLineSegment(sketch, "E74.top", {"start": v(-33, -115.08) * mm, "end": v(-34, -115.08) * mm});
            skLineSegment(sketch, "E74.left", {"start": v(-33, -102.08) * mm, "end": v(-33, -115.08) * mm});
            skLineSegment(sketch, "E74.right", {"start": v(-34, -102.08) * mm, "end": v(-34, -115.08) * mm});
            skLineSegment(sketch, "E75.bottom", {"start": v(-43, -114.08) * mm, "end": v(-34, -114.08) * mm});
            skLineSegment(sketch, "E75.top", {"start": v(-43, -115.08) * mm, "end": v(-34, -115.08) * mm});
            skLineSegment(sketch, "E75.left", {"start": v(-43, -114.08) * mm, "end": v(-43, -115.08) * mm});
            skLineSegment(sketch, "E75.right", {"start": v(-34, -114.08) * mm, "end": v(-34, -115.08) * mm});
            skSolve(sketch);
        }
        {
            var Q0;
            Q0=qSketchRegion(id+"F23",true);
            extrude(context, id + "F24", {"entities" : qUnion([Q0]), "operationType" : NewBodyOperationType.ADD, "depth" : 4 * mm});
        }
        {
            var Q0;
            {var subQ0=sQuery(id+"F0.wireOp",EDGE,"E3");Q0=makeQuery(id+"FKRJtqk0ZjomfcX_7.boolean.opBoolean","SPLIT",FACE,{"disambiguationData":[TD([makeQuery(id+"F1.opExtrude","SWEPT_FACE",FACE,{"disambiguationData":[OSD([subQ0])]})])],"derivedFrom":makeQuery(id+"F1.opExtrude","CAP_FACE",FACE,{"disambiguationData":[OSD([sQuery(id+"F0.wireOp",EDGE,"E0.bottom"),sQuery(id+"F0.wireOp",EDGE,"E0.top"),sQuery(id+"F0.wireOp",EDGE,"E0.left"),sQuery(id+"F0.wireOp",EDGE,"E0.right"),sQuery(id+"F0.wireOp",EDGE,"E1"),sQuery(id+"F0.wireOp",EDGE,"E2"),subQ0,sQuery(id+"F0.wireOp",EDGE,"E4.bottom"),sQuery(id+"F0.wireOp",EDGE,"E4.top"),sQuery(id+"F0.wireOp",EDGE,"E4.left"),sQuery(id+"F0.wireOp",EDGE,"E4.right"),sQuery(id+"F0.wireOp",EDGE,"E11.left"),sQuery(id+"F0.wireOp",EDGE,"E11.right")])],"isStart":false})});}
            extrude(context, id + "F25", {"entities" : qUnion([Q0]), "operationType" : NewBodyOperationType.ADD, "depth" : 1 * mm});
        }
        {
            var Q0;
            Q0=sQuery(id+"F22.wireOp",VERTEX,"E67.center");
            var Q1;
            Q1=sQuery(id+"F22.wireOp",VERTEX,"E68.center");
            var Q2;
            Q2=makeQuery(id+"F1.opExtrude","SWEPT_BODY",BODY,{"disambiguationData":[OSD([sQuery(id+"F0.wireOp",EDGE,"E0.bottom"),sQuery(id+"F0.wireOp",EDGE,"E0.top"),sQuery(id+"F0.wireOp",EDGE,"E0.left"),sQuery(id+"F0.wireOp",EDGE,"E0.right"),sQuery(id+"F0.wireOp",EDGE,"E1"),sQuery(id+"F0.wireOp",EDGE,"E2"),sQuery(id+"F0.wireOp",EDGE,"E3"),sQuery(id+"F0.wireOp",EDGE,"E4.bottom"),sQuery(id+"F0.wireOp",EDGE,"E4.top"),sQuery(id+"F0.wireOp",EDGE,"E4.left"),sQuery(id+"F0.wireOp",EDGE,"E4.right"),sQuery(id+"F0.wireOp",EDGE,"E11.left"),sQuery(id+"F0.wireOp",EDGE,"E11.right")])]});
            hole(context, id + "F26", {"style" : HoleStyle.SIMPLE, "endStyle" : HoleEndStyle.THROUGH, "holeDiameter" : 1.4 * mm, "isTappedThrough" : true, "tappedDepth" : 12 * mm, "tapClearance" : 3, "locations" : qUnion([Q0, Q1]), "scope" : qUnion([Q2])});
        }
        {
            var Q0;
            {var subQ0=sQuery(id+"F2.wireOp",EDGE,"E37.top");var subQ1=sQuery(id+"F2.wireOp",EDGE,"E37.bottom");var subQ2=sQuery(id+"F2.wireOp",EDGE,"E36.right");var subQ3=sQuery(id+"F2.wireOp",EDGE,"E36.left");Q0=makeQuery(id+"F13.boolean.opBoolean","MERGE",FACE,{"derivedFrom":[makeQuery(id+"F11.opExtrude","CAP_FACE",FACE,{"disambiguationData":[OSD([sQuery(id+"F2.wireOp",EDGE,"E30.bottom"),sQuery(id+"F2.wireOp",EDGE,"E30.top"),sQuery(id+"F2.wireOp",EDGE,"E30.left"),sQuery(id+"F2.wireOp",EDGE,"E30.right"),sQuery(id+"F2.wireOp",EDGE,"E35.bottom"),sQuery(id+"F2.wireOp",EDGE,"E35.top"),sQuery(id+"F2.wireOp",EDGE,"E35.left"),sQuery(id+"F2.wireOp",EDGE,"E35.right"),subQ3,subQ2,subQ1,subQ0])],"isStart":true}),makeQuery(id+"F13.opExtrude","CAP_FACE",FACE,{"disambiguationData":[OSD([sQuery(id+"F2.wireOp",EDGE,"E36.bottom"),sQuery(id+"F2.wireOp",EDGE,"E36.top"),subQ3,subQ2,subQ1,subQ0,sQuery(id+"F2.wireOp",EDGE,"E37.left"),sQuery(id+"F2.wireOp",EDGE,"E37.right")])],"isStart":true})]});}
            var sketch = newSketch(context, id + "F27", { "sketchPlane" : qUnion([Q0])});
            skLineSegment(sketch, "E76.bottom", {"start": v(-63, 115.08) * mm, "end": v(-33, 115.08) * mm});
            skLineSegment(sketch, "E76.top", {"start": v(-63, 114.08) * mm, "end": v(-33, 114.08) * mm});
            skLineSegment(sketch, "E76.left", {"start": v(-63, 115.08) * mm, "end": v(-63, 114.08) * mm});
            skLineSegment(sketch, "E76.right", {"start": v(-33, 115.08) * mm, "end": v(-33, 114.08) * mm});
            skLineSegment(sketch, "E77.bottom", {"start": v(-63, 114.08) * mm, "end": v(-62, 114.08) * mm});
            skLineSegment(sketch, "E77.top", {"start": v(-63, 101.08) * mm, "end": v(-62, 101.08) * mm});
            skLineSegment(sketch, "E77.left", {"start": v(-63, 114.08) * mm, "end": v(-63, 101.08) * mm});
            skLineSegment(sketch, "E77.right", {"start": v(-62, 114.08) * mm, "end": v(-62, 101.08) * mm});
            skLineSegment(sketch, "E78.bottom", {"start": v(-62, 101.08) * mm, "end": v(-33, 101.08) * mm});
            skLineSegment(sketch, "E78.top", {"start": v(-62, 102.08) * mm, "end": v(-33, 102.08) * mm});
            skLineSegment(sketch, "E78.left", {"start": v(-62, 101.08) * mm, "end": v(-62, 102.08) * mm});
            skLineSegment(sketch, "E78.right", {"start": v(-33, 101.08) * mm, "end": v(-33, 102.08) * mm});
            skLineSegment(sketch, "E79.bottom", {"start": v(-33, 114.08) * mm, "end": v(-34, 114.08) * mm});
            skLineSegment(sketch, "E79.top", {"start": v(-33, 102.08) * mm, "end": v(-34, 102.08) * mm});
            skLineSegment(sketch, "E79.left", {"start": v(-33, 114.08) * mm, "end": v(-33, 102.08) * mm});
            skLineSegment(sketch, "E79.right", {"start": v(-34, 114.08) * mm, "end": v(-34, 102.08) * mm});
            skSolve(sketch);
        }
        {
            var Q0;
            Q0=sQuery(id+"F22.wireOp",VERTEX,"E67.center");
            var Q1;
            Q1=sQuery(id+"F22.wireOp",VERTEX,"E68.center");
            var Q2;
            Q2=makeQuery(id+"F1.opExtrude","SWEPT_BODY",BODY,{"disambiguationData":[OSD([sQuery(id+"F0.wireOp",EDGE,"E0.bottom"),sQuery(id+"F0.wireOp",EDGE,"E0.top"),sQuery(id+"F0.wireOp",EDGE,"E0.left"),sQuery(id+"F0.wireOp",EDGE,"E0.right"),sQuery(id+"F0.wireOp",EDGE,"E1"),sQuery(id+"F0.wireOp",EDGE,"E2"),sQuery(id+"F0.wireOp",EDGE,"E3"),sQuery(id+"F0.wireOp",EDGE,"E4.bottom"),sQuery(id+"F0.wireOp",EDGE,"E4.top"),sQuery(id+"F0.wireOp",EDGE,"E4.left"),sQuery(id+"F0.wireOp",EDGE,"E4.right"),sQuery(id+"F0.wireOp",EDGE,"E11.left"),sQuery(id+"F0.wireOp",EDGE,"E11.right")])]});
            hole(context, id + "F28", {"style" : HoleStyle.SIMPLE, "endStyle" : HoleEndStyle.THROUGH, "oppositeDirection" : true, "holeDiameter" : 1.4 * mm, "isTappedThrough" : true, "tappedDepth" : 12 * mm, "tapClearance" : 3, "locations" : qUnion([Q0, Q1]), "scope" : qUnion([Q2])});
        }
        {
            var Q0;
            Q0=qSketchRegion(id+"F27",true);
            extrude(context, id + "F29", {"entities" : qUnion([Q0]), "operationType" : NewBodyOperationType.ADD, "depth" : 3 * mm});
        }
        {
            var Q0;
            Q0=makeQuery(id+"F22.imprint","IMPRINT",FACE,{"disambiguationData":[TD([[makeQuery(id+"F22.imprint","IMPRINT",EDGE,{"derivedFrom":sQuery(id+"F22.wireOp",EDGE,"E62")}),-1.0]])]});
            extrude(context, id + "F30", {"entities" : qUnion([Q0]), "operationType" : NewBodyOperationType.ADD, "depth" : 5 * mm});
        }
        {
            var Q0;
            Q0=makeQuery(id+"F1.opExtrude","CAP_FACE",FACE,{"disambiguationData":[OSD([sQuery(id+"F0.wireOp",EDGE,"E0.bottom"),sQuery(id+"F0.wireOp",EDGE,"E0.top"),sQuery(id+"F0.wireOp",EDGE,"E0.left"),sQuery(id+"F0.wireOp",EDGE,"E0.right"),sQuery(id+"F0.wireOp",EDGE,"E1"),sQuery(id+"F0.wireOp",EDGE,"E2"),sQuery(id+"F0.wireOp",EDGE,"E3"),sQuery(id+"F0.wireOp",EDGE,"E4.bottom"),sQuery(id+"F0.wireOp",EDGE,"E4.top"),sQuery(id+"F0.wireOp",EDGE,"E4.left"),sQuery(id+"F0.wireOp",EDGE,"E4.right"),sQuery(id+"F0.wireOp",EDGE,"E11.left"),sQuery(id+"F0.wireOp",EDGE,"E11.right")])],"isStart":true});
            var sketch = newSketch(context, id + "F31", { "sketchPlane" : qUnion([Q0])});
            skLineSegment(sketch, "E80.bottom", {"start": v(-25.5, 28) * mm, "end": v(25.5, 28) * mm});
            skLineSegment(sketch, "E80.top", {"start": v(-25.5, 27.8) * mm, "end": v(25.5, 27.8) * mm});
            skLineSegment(sketch, "E80.left", {"start": v(-25.5, 28) * mm, "end": v(-25.5, 27.8) * mm});
            skLineSegment(sketch, "E80.right", {"start": v(25.5, 28) * mm, "end": v(25.5, 27.8) * mm});
            skLineSegment(sketch, "E81.bottom", {"start": v(-25.5, -28) * mm, "end": v(25.5, -28) * mm});
            skLineSegment(sketch, "E81.top", {"start": v(-25.5, -27.8) * mm, "end": v(25.5, -27.8) * mm});
            skLineSegment(sketch, "E81.left", {"start": v(-25.5, -28) * mm, "end": v(-25.5, -27.8) * mm});
            skLineSegment(sketch, "E81.right", {"start": v(25.5, -28) * mm, "end": v(25.5, -27.8) * mm});
            skLineSegment(sketch, "E82.bottom", {"start": v(-25.5, -27.8) * mm, "end": v(-25.3, -27.8) * mm});
            skLineSegment(sketch, "E82.top", {"start": v(-25.5, 27.8) * mm, "end": v(-25.3, 27.8) * mm});
            skLineSegment(sketch, "E82.left", {"start": v(-25.5, -27.8) * mm, "end": v(-25.5, 27.8) * mm});
            skLineSegment(sketch, "E82.right", {"start": v(-25.3, -27.8) * mm, "end": v(-25.3, 27.8) * mm});
            skLineSegment(sketch, "E83.bottom", {"start": v(25.5, -27.8) * mm, "end": v(25.3, -27.8) * mm});
            skLineSegment(sketch, "E83.top", {"start": v(25.5, 27.8) * mm, "end": v(25.3, 27.8) * mm});
            skLineSegment(sketch, "E83.left", {"start": v(25.5, -27.8) * mm, "end": v(25.5, 27.8) * mm});
            skLineSegment(sketch, "E83.right", {"start": v(25.3, -27.8) * mm, "end": v(25.3, 27.8) * mm});
            skSolve(sketch);
        }
        {
            var Q0;
            Q0=qSketchRegion(id+"F31",true);
            extrude(context, id + "F32", {"entities" : qUnion([Q0]), "operationType" : NewBodyOperationType.REMOVE, "oppositeDirection" : true, "depth" : 25 * mm});
        }
        {
            var Q0;
            Q0=sQuery(id+"F22.wireOp",VERTEX,"E67.center");
            var Q1;
            Q1=sQuery(id+"F22.wireOp",VERTEX,"E68.center");
            var Q2;
            Q2=makeQuery(id+"F1.opExtrude","SWEPT_BODY",BODY,{"disambiguationData":[OSD([sQuery(id+"F0.wireOp",EDGE,"E0.bottom"),sQuery(id+"F0.wireOp",EDGE,"E0.top"),sQuery(id+"F0.wireOp",EDGE,"E0.left"),sQuery(id+"F0.wireOp",EDGE,"E0.right"),sQuery(id+"F0.wireOp",EDGE,"E1"),sQuery(id+"F0.wireOp",EDGE,"E2"),sQuery(id+"F0.wireOp",EDGE,"E3"),sQuery(id+"F0.wireOp",EDGE,"E4.bottom"),sQuery(id+"F0.wireOp",EDGE,"E4.top"),sQuery(id+"F0.wireOp",EDGE,"E4.left"),sQuery(id+"F0.wireOp",EDGE,"E4.right"),sQuery(id+"F0.wireOp",EDGE,"E11.left"),sQuery(id+"F0.wireOp",EDGE,"E11.right")])]});
            hole(context, id + "F33", {"style" : HoleStyle.SIMPLE, "endStyle" : HoleEndStyle.THROUGH, "oppositeDirection" : true, "holeDiameter" : 1.6 * mm, "isTappedThrough" : true, "tappedDepth" : 12 * mm, "tapClearance" : 3, "locations" : qUnion([Q0, Q1]), "scope" : qUnion([Q2])});
        }
        {
            var Q0;
            Q0=sQuery(id+"F22.wireOp",VERTEX,"E68.center");
            var Q1;
            Q1=sQuery(id+"F22.wireOp",VERTEX,"E67.center");
            var Q2;
            Q2=makeQuery(id+"F1.opExtrude","SWEPT_BODY",BODY,{"disambiguationData":[OSD([sQuery(id+"F0.wireOp",EDGE,"E0.bottom"),sQuery(id+"F0.wireOp",EDGE,"E0.top"),sQuery(id+"F0.wireOp",EDGE,"E0.left"),sQuery(id+"F0.wireOp",EDGE,"E0.right"),sQuery(id+"F0.wireOp",EDGE,"E1"),sQuery(id+"F0.wireOp",EDGE,"E2"),sQuery(id+"F0.wireOp",EDGE,"E3"),sQuery(id+"F0.wireOp",EDGE,"E4.bottom"),sQuery(id+"F0.wireOp",EDGE,"E4.top"),sQuery(id+"F0.wireOp",EDGE,"E4.left"),sQuery(id+"F0.wireOp",EDGE,"E4.right"),sQuery(id+"F0.wireOp",EDGE,"E11.left"),sQuery(id+"F0.wireOp",EDGE,"E11.right")])]});
            hole(context, id + "F34", {"style" : HoleStyle.SIMPLE, "endStyle" : HoleEndStyle.THROUGH, "holeDiameter" : 1.6 * mm, "isTappedThrough" : true, "tappedDepth" : 12 * mm, "tapClearance" : 3, "locations" : qUnion([Q0, Q1]), "scope" : qUnion([Q2])});
        }
    });
